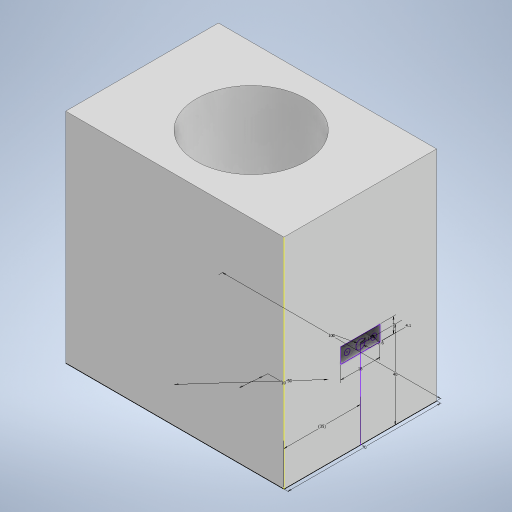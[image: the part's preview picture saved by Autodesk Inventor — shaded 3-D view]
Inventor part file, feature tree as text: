
AUTODESK INVENTOR PART (.ipt)
format: ipt  version: 2024 (Build 280153000, 153)  size: 224,256 bytes
history: native  units: mm
features: extrude x4, sketch x2, hole x2, other x1
ambient origin geometry x8: Origin, YZ Plane, XZ Plane, XY Plane, X Axis, Y Axis, Z Axis, Center Point
bodies: Body1 (feature_tree)
feature tree (9):
  other  "實體1"
  sketch  "草圖1"
  extrude  "擠出1"  Depth=100.0mm
  extrude  "擠出2"  Depth=70.0mm
  extrude  "擠出3"  Depth=50.0mm
  sketch  "草圖2"
  hole  "孔1"  [1 undecoded]
  extrude  "擠出4"  Depth=15.0mm TaperAngle=0.0deg
  hole  "孔2"  [1 undecoded]
note: 2 required parameter values undecoded (feature->parameter linkage not recoverable at this tier; creation-order binding heuristic only, values carry confidence <= 0.55)
